# Revit family: Curved Walls Light Cove
name_source: partatom
category: Generic Models
revit_build: Autodesk Revit 2016 (Build: 20150714_1515(x64)
units: mm (PartAtom-declared; Revit-internal decimal feet)

## family parameters
Always vertical = No
Can host rebar = No
Cut with Voids When Loaded = No
Part Type = Normal
Room Calculation Point = No
Round Connector Dimension = Use Diameter
Shared = No
Work Plane-Based = Yes

## types (2) — shared parameters
Default Elevation = 0' - 0"
Description = Prefabricated Drywall Profiles
GWB Thickness (1/2") = 0' - 0 1/2"
Manufacturer = Curved Walls Inc
Straight Transition Length B = 0' - 4"
URL = www.curvedwalls.ca

## per-type parameters (varying)
| type | Cove Radius (6" & 12" Standard) | Overall Dimension A | Overall Dimension B | Straight Transition Length A |
| 1/4" Thk. x Custom R x 15" W x 12" H | 0' - 8" | 1' - 3" | 1' - 0" | 0' - 7" |
| 1/2" Thk. x 12" R x 16" W x 16" H | 1' - 0" | 1' - 4" | 1' - 4" | 0' - 4" |

## geometry (parser evidence)
native form markers: Blend x4, Sweep x2
no freeform markers — native parametric forms only
